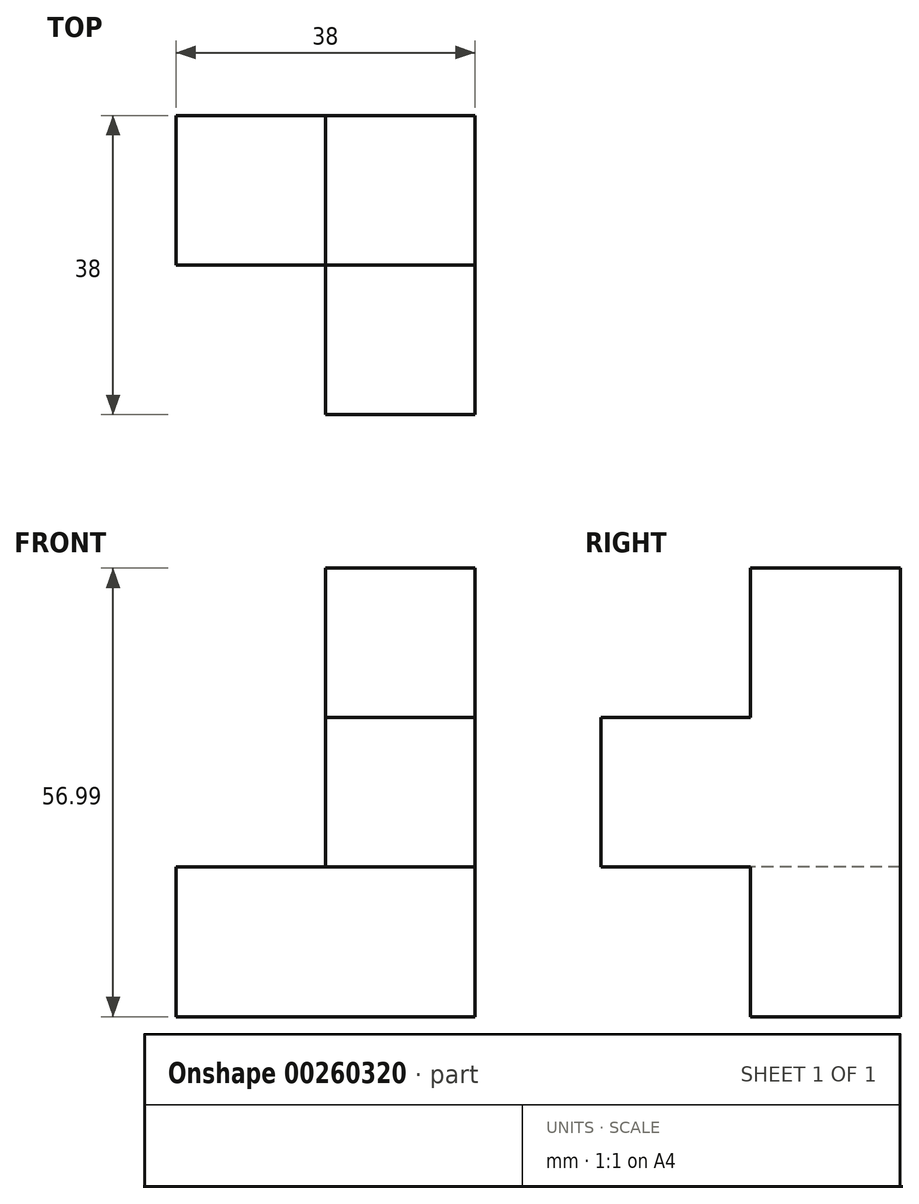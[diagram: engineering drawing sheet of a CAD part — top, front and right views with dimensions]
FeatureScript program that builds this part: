
annotation { "Feature Type Name" : "Feature", "Feature Type Description" : "" }
export const myFeature = defineFeature(function(context is Context, id is Id, definition is map)
    precondition{}
    {
        {
            var Q0;
            Q0=qCreatedBy(makeId("Right.planeOp"),FACE);
            var sketch = newSketch(context, id + "F0", { "sketchPlane" : qUnion([Q0])});
            skLineSegment(sketch, "E0.bottom", {"start": v(0, 0) * mm, "end": v(-19, 0) * mm});
            skLineSegment(sketch, "E0.top", {"start": v(0, -19) * mm, "end": v(-19, -19) * mm});
            skLineSegment(sketch, "E0.left", {"start": v(0, 0) * mm, "end": v(0, -19) * mm});
            skLineSegment(sketch, "E0.right", {"start": v(-19, 0) * mm, "end": v(-19, -19) * mm});
            skLineSegment(sketch, "E1.bottom", {"start": v(0, 0) * mm, "end": v(19, 0) * mm});
            skLineSegment(sketch, "E1.top", {"start": v(0, 19) * mm, "end": v(19, 19) * mm});
            skLineSegment(sketch, "E1.left", {"start": v(0, 0) * mm, "end": v(0, 19) * mm});
            skLineSegment(sketch, "E1.right", {"start": v(19, 0) * mm, "end": v(19, 19) * mm});
            skLineSegment(sketch, "E2.top", {"start": v(0, -19) * mm, "end": v(19, -19) * mm});
            skLineSegment(sketch, "E2.right", {"start": v(19, 0) * mm, "end": v(19, -19) * mm});
            skLineSegment(sketch, "E3.top", {"start": v(0, -38) * mm, "end": v(19, -38) * mm});
            skLineSegment(sketch, "E3.left", {"start": v(0, -19) * mm, "end": v(0, -38) * mm});
            skLineSegment(sketch, "E3.right", {"start": v(19, -19) * mm, "end": v(19, -38) * mm});
            skSolve(sketch);
        }
        {
            var Q0;
            Q0=makeQuery(id+"F0.imprint","IMPRINT",FACE,{"disambiguationData":[TD([[makeQuery(id+"F0.imprint","IMPRINT",EDGE,{"derivedFrom":sQuery(id+"F0.wireOp",EDGE,"E2.top")}),-1.0]])]});
            extrude(context, id + "F1", {"entities" : qUnion([Q0]), "oppositeDirection" : true, "depth" : 38 * mm});
        }
        {
            var Q0;
            Q0 = qSketchRegion(id + "F0", true);
            extrude(context, id + "F2", {"entities" : qUnion([Q0]), "operationType" : NewBodyOperationType.ADD, "oppositeDirection" : true, "depth" : 19 * mm});
        }
    });
